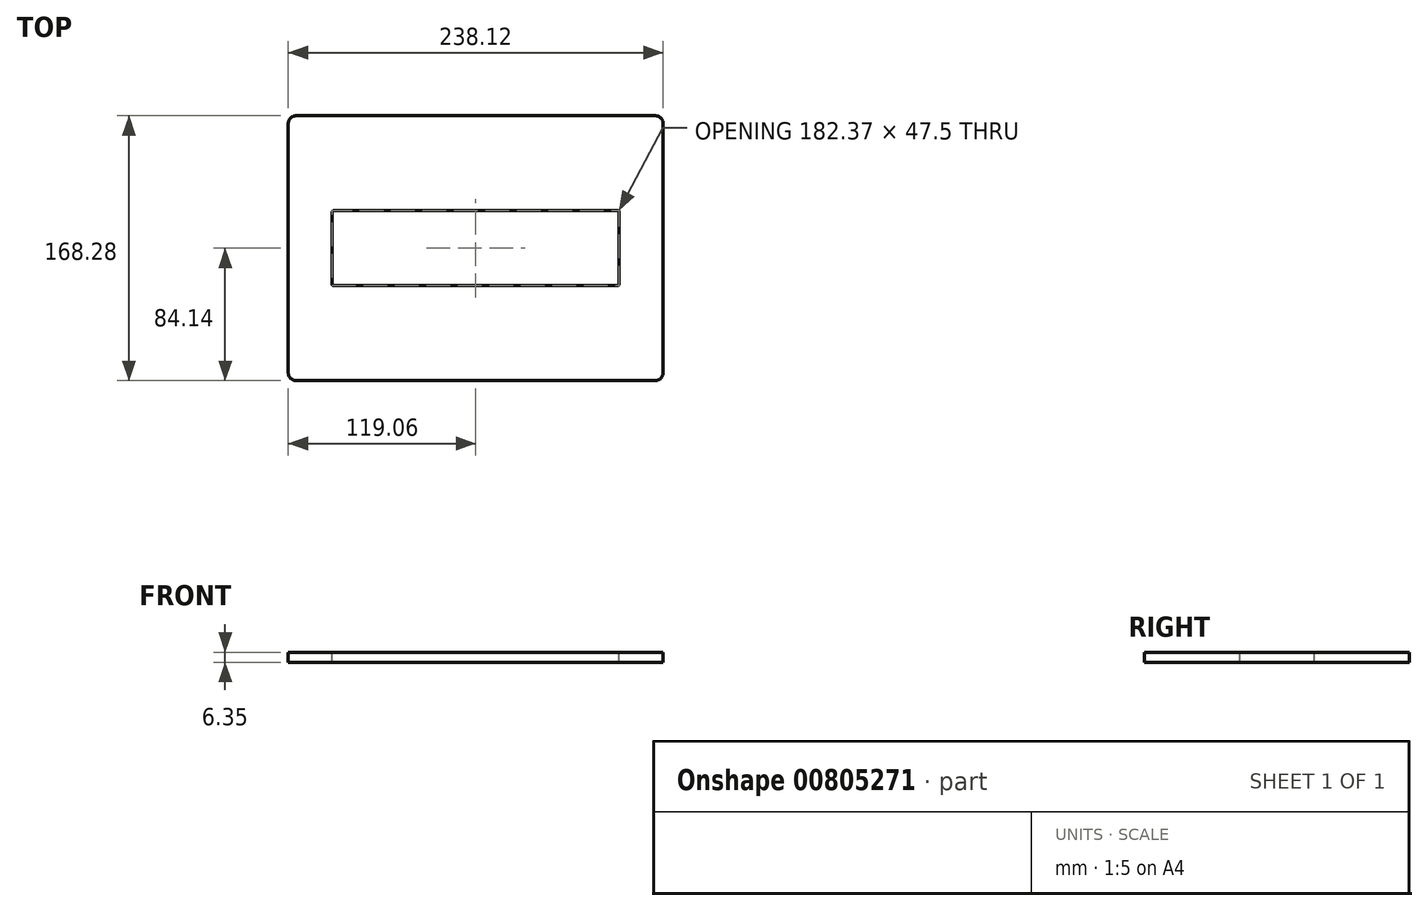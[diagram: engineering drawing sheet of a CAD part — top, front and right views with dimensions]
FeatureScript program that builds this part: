
annotation { "Feature Type Name" : "Feature", "Feature Type Description" : "" }
export const myFeature = defineFeature(function(context is Context, id is Id, definition is map)
    precondition{}
    {
        {
            var Q0;
            Q0=qCreatedBy(makeId("Top.planeOp"),FACE);
            var sketch = newSketch(context, id + "F0", { "sketchPlane" : qUnion([Q0])});
            skLineSegment(sketch, "E0.bottom", {"start": v(-119.06, 84.14) * mm, "end": v(119.06, 84.14) * mm});
            skLineSegment(sketch, "E0.top", {"start": v(-119.06, -84.14) * mm, "end": v(119.06, -84.14) * mm});
            skLineSegment(sketch, "E0.left", {"start": v(-119.06, 84.14) * mm, "end": v(-119.06, -84.14) * mm});
            skLineSegment(sketch, "E0.right", {"start": v(119.06, 84.14) * mm, "end": v(119.06, -84.14) * mm});
            skPoint(sketch, "E0.middle", {"position": v(0, 0) * mm});
            skSolve(sketch);
        }
        {
            var Q0;
            Q0 = qSketchRegion(id + "F0", true);
            extrude(context, id + "F1", {"entities" : qUnion([Q0]), "depth" : 6.35 * mm, "offsetDistance" : 25.4 * mm});
        }
        {
            var Q0;
            Q0=makeQuery(id+"F1.opExtrude","CAP_FACE",FACE,{"disambiguationData":[OSD([sQuery(id+"F0.wireOp",EDGE,"E0.bottom"),sQuery(id+"F0.wireOp",EDGE,"E0.top"),sQuery(id+"F0.wireOp",EDGE,"E0.left"),sQuery(id+"F0.wireOp",EDGE,"E0.right")])],"isStart":false});
            var sketch = newSketch(context, id + "F2", { "sketchPlane" : qUnion([Q0])});
            skLineSegment(sketch, "E1.bottom", {"start": v(-89.92, 22.48) * mm, "end": v(89.92, 22.48) * mm});
            skLineSegment(sketch, "E1.top", {"start": v(-89.92, -22.48) * mm, "end": v(89.92, -22.48) * mm});
            skLineSegment(sketch, "E1.left", {"start": v(-89.92, 22.48) * mm, "end": v(-89.92, -22.48) * mm});
            skLineSegment(sketch, "E1.right", {"start": v(89.92, 22.48) * mm, "end": v(89.92, -22.48) * mm});
            skPoint(sketch, "E1.middle", {"position": v(0, 0) * mm});
            skSolve(sketch);
        }
        {
            var Q0;
            Q0 = qSketchRegion(id + "F2", true);
            extrude(context, id + "F3", {"entities" : qUnion([Q0]), "operationType" : NewBodyOperationType.REMOVE, "oppositeDirection" : true, "depth" : 25.4 * mm, "offsetDistance" : 25.4 * mm});
        }
        {
            var Q0;
            Q0=makeQuery(id+"F1.opExtrude","CAP_FACE",FACE,{"disambiguationData":[OSD([sQuery(id+"F0.wireOp",EDGE,"E0.bottom"),sQuery(id+"F0.wireOp",EDGE,"E0.top"),sQuery(id+"F0.wireOp",EDGE,"E0.left"),sQuery(id+"F0.wireOp",EDGE,"E0.right")])],"isStart":false});
            var sketch = newSketch(context, id + "F4", { "sketchPlane" : qUnion([Q0])});
            skLineSegment(sketch, "E2.0", {"start": v(-90.4, 23.75) * mm, "end": v(90.4, 23.75) * mm});
            skLineSegment(sketch, "E2.1", {"start": v(-91.19, 22.96) * mm, "end": v(-91.19, -22.96) * mm});
            skLineSegment(sketch, "E2.2", {"start": v(-90.4, -23.75) * mm, "end": v(90.4, -23.75) * mm});
            skLineSegment(sketch, "E2.3", {"start": v(91.19, 22.96) * mm, "end": v(91.19, -22.96) * mm});
            skPoint(sketch, "E3.visualSharp", {"position": v(-91.19, 23.75) * mm});
            skArc(sketch, "E3.filletArc", {"start": v(-90.4, 23.75) * mm, "mid": v(-90.96, 23.52) * mm, "end": v(-91.19, 22.96) * mm});
            skPoint(sketch, "E4.visualSharp", {"position": v(-91.19, -23.75) * mm});
            skArc(sketch, "E4.filletArc", {"start": v(-91.19, -22.96) * mm, "mid": v(-90.96, -23.52) * mm, "end": v(-90.4, -23.75) * mm});
            skPoint(sketch, "E5.visualSharp", {"position": v(91.19, -23.75) * mm});
            skArc(sketch, "E5.filletArc", {"start": v(90.4, -23.75) * mm, "mid": v(90.96, -23.52) * mm, "end": v(91.19, -22.96) * mm});
            skPoint(sketch, "E6.visualSharp", {"position": v(91.19, 23.75) * mm});
            skArc(sketch, "E6.filletArc", {"start": v(91.19, 22.96) * mm, "mid": v(90.96, 23.52) * mm, "end": v(90.4, 23.75) * mm});
            skSolve(sketch);
        }
        {
            var Q0;
            Q0 = qSketchRegion(id + "F4", true);
            extrude(context, id + "F5", {"entities" : qUnion([Q0]), "operationType" : NewBodyOperationType.REMOVE, "endBound" : BoundingType.THROUGH_ALL, "oppositeDirection" : true, "depth" : 25.4 * mm, "offsetDistance" : 25.4 * mm});
        }
        {
            var Q0;
            Q0=makeQuery(id+"F1.opExtrude","SWEPT_EDGE",EDGE,{"disambiguationData":[OSD([sQuery(id+"F0.wireOp",EDGE,"E0.top"),sQuery(id+"F0.wireOp",EDGE,"E0.right")])]});
            var Q1;
            Q1=makeQuery(id+"F1.opExtrude","SWEPT_EDGE",EDGE,{"disambiguationData":[OSD([sQuery(id+"F0.wireOp",EDGE,"E0.bottom"),sQuery(id+"F0.wireOp",EDGE,"E0.right")])]});
            var Q2;
            Q2=makeQuery(id+"F1.opExtrude","SWEPT_EDGE",EDGE,{"disambiguationData":[OSD([sQuery(id+"F0.wireOp",EDGE,"E0.top"),sQuery(id+"F0.wireOp",EDGE,"E0.left")])]});
            var Q3;
            Q3=makeQuery(id+"F1.opExtrude","SWEPT_EDGE",EDGE,{"disambiguationData":[OSD([sQuery(id+"F0.wireOp",EDGE,"E0.bottom"),sQuery(id+"F0.wireOp",EDGE,"E0.left")])]});
            fillet(context, id + "F6", {"entities" : qUnion([Q0, Q1, Q2, Q3]), "radius" : 5.08 * mm, "tangentPropagation" : true, "allowEdgeOverflow" : false});
        }
    });
